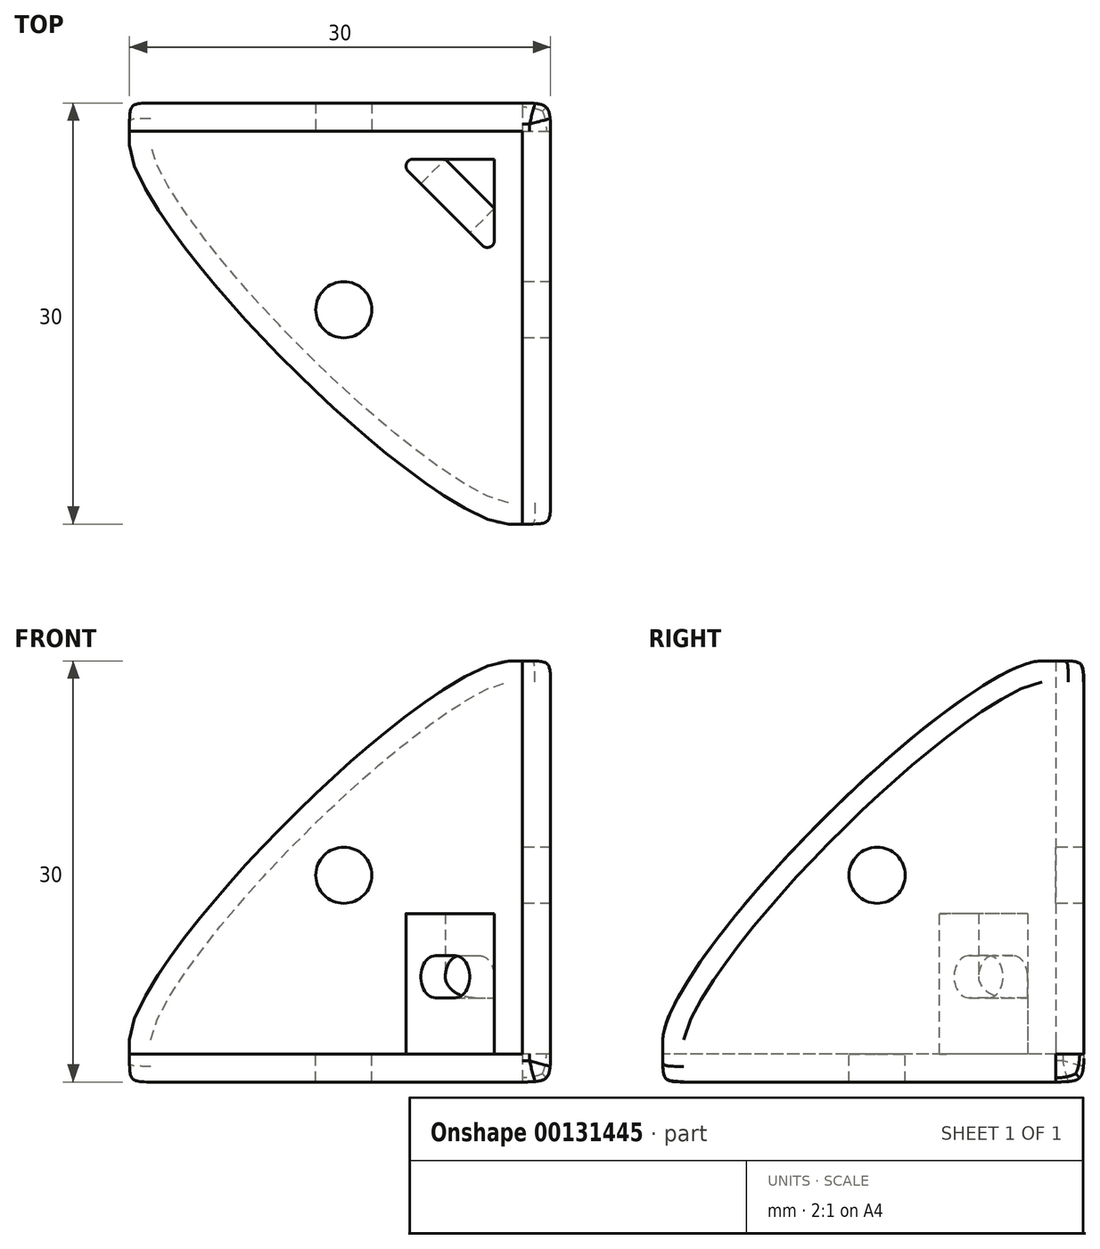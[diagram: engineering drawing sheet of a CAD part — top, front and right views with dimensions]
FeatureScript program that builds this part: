
annotation { "Feature Type Name" : "Feature", "Feature Type Description" : "" }
export const myFeature = defineFeature(function(context is Context, id is Id, definition is map)
    precondition{}
    {
        {
            var Q0;
            Q0=qCreatedBy(makeId("Top.planeOp"),FACE);
            var sketch = newSketch(context, id + "F0", { "sketchPlane" : qUnion([Q0])});
            skLineSegment(sketch, "E0.bottom", {"start": v(0, 0) * mm, "end": v(-30, 0) * mm});
            skLineSegment(sketch, "E0.top", {"start": v(0, -30) * mm, "end": v(-30, -30) * mm});
            skLineSegment(sketch, "E0.left", {"start": v(0, 0) * mm, "end": v(0, -30) * mm});
            skLineSegment(sketch, "E0.right", {"start": v(-30, 0) * mm, "end": v(-30, -30) * mm});
            skSolve(sketch);
        }
        {
            var Q0;
            Q0 = qSketchRegion(id + "F0", true);
            extrude(context, id + "F1", {"entities" : qUnion([Q0]), "depth" : 30 * mm});
        }
        {
            var Q0;
            Q0=makeQuery(id+"F1.opExtrude","CAP_FACE",FACE,{"disambiguationData":[OSD([sQuery(id+"F0.wireOp",EDGE,"E0.bottom"),sQuery(id+"F0.wireOp",EDGE,"E0.top"),sQuery(id+"F0.wireOp",EDGE,"E0.left"),sQuery(id+"F0.wireOp",EDGE,"E0.right")])],"isStart":false});
            var Q1;
            Q1=makeQuery(id+"F1.opExtrude","SWEPT_FACE",FACE,{"disambiguationData":[OSD([sQuery(id+"F0.wireOp",EDGE,"E0.right")])]});
            var Q2;
            Q2=makeQuery(id+"F1.opExtrude","SWEPT_FACE",FACE,{"disambiguationData":[OSD([sQuery(id+"F0.wireOp",EDGE,"E0.top")])]});
            shell(context, id + "F2", {"entities" : qUnion([Q0, Q1, Q2]), "thickness" : 2 * mm});
        }
        {
            var Q0;
            Q0=makeQuery(id+"F1.opExtrude","CAP_EDGE",EDGE,{"disambiguationData":[OSD([sQuery(id+"F0.wireOp",EDGE,"E0.right")])],"isStart":false});
            var Q1;
            Q1=makeQuery(id+"F1.opExtrude","CAP_EDGE",EDGE,{"disambiguationData":[OSD([sQuery(id+"F0.wireOp",EDGE,"E0.top")])],"isStart":false});
            var Q2;
            Q2=makeQuery(id+"F1.opExtrude","SWEPT_EDGE",EDGE,{"disambiguationData":[OSD([sQuery(id+"F0.wireOp",EDGE,"E0.top"),sQuery(id+"F0.wireOp",EDGE,"E0.right")])]});
            fillet(context, id + "F3", {"entities" : qUnion([Q0, Q1, Q2]), "radius" : 27 * mm, "tangentPropagation" : true, "rho" : 0.16, "crossSection" : FilletCrossSection.CONIC, "allowEdgeOverflow" : false});
        }
        {
            var Q0;
            Q0=makeQuery(id+"F1.opExtrude","CAP_EDGE",EDGE,{"disambiguationData":[OSD([sQuery(id+"F0.wireOp",EDGE,"E0.bottom")])],"isStart":true});
            var Q1;
            Q1=makeQuery(id+"F1.opExtrude","CAP_EDGE",EDGE,{"disambiguationData":[OSD([sQuery(id+"F0.wireOp",EDGE,"E0.left")])],"isStart":true});
            var Q2;
            Q2=makeQuery(id+"F1.opExtrude","SWEPT_EDGE",EDGE,{"disambiguationData":[OSD([sQuery(id+"F0.wireOp",EDGE,"E0.bottom"),sQuery(id+"F0.wireOp",EDGE,"E0.left")])]});
            fillet(context, id + "F4", {"entities" : qUnion([Q0, Q1, Q2]), "radius" : 2 * mm, "tangentPropagation" : true, "rho" : 0.7, "crossSection" : FilletCrossSection.CONIC, "allowEdgeOverflow" : false});
        }
        {
            var Q0;
            Q0=makeQuery(id+"F2.opShell","OFFSET_FACE",FACE,{"disambiguationData":[OSD([sQuery(id+"F0.wireOp",EDGE,"E0.bottom"),sQuery(id+"F0.wireOp",EDGE,"E0.top"),sQuery(id+"F0.wireOp",EDGE,"E0.left"),sQuery(id+"F0.wireOp",EDGE,"E0.right")])]});
            var sketch = newSketch(context, id + "F5", { "sketchPlane" : qUnion([Q0])});
            skLineSegment(sketch, "E1.0", {"start": v(-2, -2) * mm, "end": v(-30, -2) * mm});
            skLineSegment(sketch, "E2.0", {"start": v(-2, -2) * mm, "end": v(-2, -30) * mm});
            skLineSegment(sketch, "E3", {"start": v(-11, -4) * mm, "end": v(-4, -4) * mm});
            skLineSegment(sketch, "E4", {"start": v(-4, -4) * mm, "end": v(-4, -11) * mm});
            skLineSegment(sketch, "E5", {"start": v(-11, -4) * mm, "end": v(-4, -11) * mm});
            skSolve(sketch);
        }
        {
            var Q0;
            Q0=makeQuery(id+"F5.imprint","IMPRINT",FACE,{"disambiguationData":[TD([[makeQuery(id+"F5.imprint","IMPRINT",EDGE,{"derivedFrom":sQuery(id+"F5.wireOp",EDGE,"E3")}),-1.0]])]});
            extrude(context, id + "F6", {"entities" : qUnion([Q0]), "operationType" : NewBodyOperationType.ADD, "depth" : 4 * mm});
        }
        {
            var Q0;
            Q0=makeQuery(id+"F6.opExtrude","CAP_FACE",FACE,{"disambiguationData":[OSD([sQuery(id+"F5.wireOp",EDGE,"E3"),sQuery(id+"F5.wireOp",EDGE,"E4"),sQuery(id+"F5.wireOp",EDGE,"E5")])],"isStart":false});
            var sketch = newSketch(context, id + "F7", { "sketchPlane" : qUnion([Q0])});
            skLineSegment(sketch, "E6.0.0", {"start": v(-4, -4) * mm, "end": v(-11, -4) * mm});
            skLineSegment(sketch, "E6.0.1", {"start": v(-11, -4) * mm, "end": v(-4, -11) * mm});
            skLineSegment(sketch, "E6.0.2", {"start": v(-4, -11) * mm, "end": v(-4, -4) * mm});
            skLineSegment(sketch, "E7", {"start": v(-7.5, -4) * mm, "end": v(-4, -7.5) * mm});
            skSolve(sketch);
        }
        {
            var Q0;
            {var subQ0=sQuery(id+"F7.wireOp",EDGE,"E6.0.1");Q0=makeQuery(id+"F7.imprint","IMPRINT",FACE,{"disambiguationData":[TD([[makeQuery(id+"F7.imprint","IMPRINT",EDGE,{"derivedFrom":subQ0}),1.0]])]});}
            extrude(context, id + "F8", {"entities" : qUnion([Q0]), "operationType" : NewBodyOperationType.ADD, "depth" : 6 * mm});
        }
        {
            var Q0;
            Q0=makeQuery(id+"F8.opExtrude","SWEPT_FACE",FACE,{"disambiguationData":[OSD([sQuery(id+"F7.wireOp",EDGE,"E7")])]});
            var sketch = newSketch(context, id + "F9", { "sketchPlane" : qUnion([Q0])});
            skLineSegment(sketch, "E8.0", {"start": v(2.47, 6) * mm, "end": v(-2.47, 6) * mm});
            skLineSegment(sketch, "E9", {"start": v(2.47, 6) * mm, "end": v(2.47, 9) * mm});
            skLineSegment(sketch, "E10", {"start": v(2.47, 9) * mm, "end": v(-2.47, 9) * mm});
            skLineSegment(sketch, "E11", {"start": v(-2.47, 9) * mm, "end": v(-2.47, 6) * mm});
            skSolve(sketch);
        }
        {
            var Q0;
            Q0=makeQuery(id+"F9.imprint","IMPRINT",FACE,{"disambiguationData":[TD([[makeQuery(id+"F9.imprint","IMPRINT",EDGE,{"derivedFrom":sQuery(id+"F9.wireOp",EDGE,"E8.0")}),-1.0]])]});
            extrude(context, id + "F10", {"entities" : qUnion([Q0]), "operationType" : NewBodyOperationType.REMOVE, "endBound" : BoundingType.THROUGH_ALL, "oppositeDirection" : true, "depth" : 25 * mm});
        }
        {
            var Q0;
            Q0=makeQuery(id+"F2.opShell","OFFSET_FACE",FACE,{"disambiguationData":[OSD([sQuery(id+"F0.wireOp",EDGE,"E0.bottom"),sQuery(id+"F0.wireOp",EDGE,"E0.top"),sQuery(id+"F0.wireOp",EDGE,"E0.left"),sQuery(id+"F0.wireOp",EDGE,"E0.right")])]});
            var sketch = newSketch(context, id + "F11", { "sketchPlane" : qUnion([Q0])});
            skCircle(sketch, "E12", {"center": v(-14.73, -14.73) * mm, "radius": 2 * mm});
            skPoint(sketch, "E13.0", {"position": v(-2, -2) * mm});
            skLineSegment(sketch, "E14", {"start": v(-2, -2) * mm, "end": v(-14.73, -14.73) * mm, "construction": true});
            skFitSpline(sketch, "E15.0", {"points": [v(-3, -2) * mm, v(-12, -2) * mm, v(-21, -2) * mm, v(-30, -2) * mm]});
            skLineSegment(sketch, "E16.0.0", {"start": v(-30, -2) * mm, "end": v(-30, -3) * mm});
            skFitSpline(sketch, "E16.0.1", {"points": [v(-30, -3) * mm, v(-30, -3.57) * mm, v(-29.76, -4.35) * mm, v(-29.28, -5.33) * mm, v(-28.96, -5.97) * mm, v(-28.56, -6.68) * mm, v(-28.06, -7.46) * mm, v(-27.29, -8.66) * mm, v(-26.33, -9.98) * mm, v(-25.2, -11.41) * mm, v(-23.3, -13.78) * mm, v(-21.12, -16.2) * mm, v(-18.66, -18.66) * mm, v(-16.2, -21.12) * mm, v(-13.77, -23.3) * mm, v(-11.4, -25.2) * mm, v(-9.97, -26.34) * mm, v(-8.65, -27.3) * mm, v(-7.44, -28.07) * mm, v(-6.67, -28.57) * mm, v(-5.96, -28.97) * mm, v(-5.32, -29.28) * mm, v(-4.34, -29.76) * mm, v(-3.57, -30) * mm, v(-3, -30) * mm]});
            skLineSegment(sketch, "E16.0.2", {"start": v(-3, -30) * mm, "end": v(-2, -30) * mm});
            skLineSegment(sketch, "E16.0.3", {"start": v(-2, -30) * mm, "end": v(-2, -2) * mm});
            skLineSegment(sketch, "E16.0.4", {"start": v(-2, -2) * mm, "end": v(-30, -2) * mm});
            skSolve(sketch);
        }
        {
            var Q0;
            Q0=makeQuery(id+"F11.imprint","IMPRINT",FACE,{"disambiguationData":[TD([[makeQuery(id+"F11.imprint","IMPRINT",EDGE,{"derivedFrom":sQuery(id+"F11.wireOp",EDGE,"E12")}),1.0]])]});
            extrude(context, id + "F12", {"entities" : qUnion([Q0]), "operationType" : NewBodyOperationType.REMOVE, "endBound" : BoundingType.THROUGH_ALL, "oppositeDirection" : true, "depth" : 25 * mm});
        }
        {
            var Q0;
            Q0=makeQuery(id+"F8.boolean.opBoolean","MERGE",EDGE,{"derivedFrom":[makeQuery(id+"F6.opExtrude","SWEPT_EDGE",EDGE,{"disambiguationData":[OSD([sQuery(id+"F5.wireOp",EDGE,"E3"),sQuery(id+"F5.wireOp",EDGE,"E5")])]}),makeQuery(id+"F8.opExtrude","SWEPT_EDGE",EDGE,{"disambiguationData":[OSD([sQuery(id+"F7.wireOp",EDGE,"E6.0.0"),sQuery(id+"F7.wireOp",EDGE,"E6.0.1")])]})]});
            var Q1;
            Q1=makeQuery(id+"F8.boolean.opBoolean","MERGE",EDGE,{"derivedFrom":[makeQuery(id+"F6.opExtrude","SWEPT_EDGE",EDGE,{"disambiguationData":[OSD([sQuery(id+"F5.wireOp",EDGE,"E4"),sQuery(id+"F5.wireOp",EDGE,"E5")])]}),makeQuery(id+"F8.opExtrude","SWEPT_EDGE",EDGE,{"disambiguationData":[OSD([sQuery(id+"F7.wireOp",EDGE,"E6.0.1"),sQuery(id+"F7.wireOp",EDGE,"E6.0.2")])]})]});
            fillet(context, id + "F13", {"entities" : qUnion([Q0, Q1]), "radius" : 0.5 * mm, "tangentPropagation" : true, "allowEdgeOverflow" : false});
        }
        {
            var Q0;
            Q0=makeQuery(id+"F3.opFillet","BLEND_EDGE",EDGE,{"blendedFrom":[makeQuery(id+"F1.opExtrude","CAP_EDGE",EDGE,{"disambiguationData":[OSD([sQuery(id+"F0.wireOp",EDGE,"E0.right")])],"isStart":false}),makeQuery(id+"F1.opExtrude","SWEPT_FACE",FACE,{"disambiguationData":[OSD([sQuery(id+"F0.wireOp",EDGE,"E0.bottom")])]})],"blendedInto":[makeQuery(id+"F1.opExtrude","SWEPT_FACE",FACE,{"disambiguationData":[OSD([sQuery(id+"F0.wireOp",EDGE,"E0.bottom")])]})]});
            fillet(context, id + "F14", {"entities" : qUnion([Q0]), "radius" : 1.5 * mm, "tangentPropagation" : true, "rho" : 0.7, "crossSection" : FilletCrossSection.CONIC, "allowEdgeOverflow" : false});
        }
        {
            var Q0;
            Q0=makeQuery(id+"F10.boolean.opBoolean","COPY",EDGE,{"derivedFrom":makeQuery(id+"F10.opExtrude","SWEPT_EDGE",EDGE,{"disambiguationData":[OSD([sQuery(id+"F7.wireOp",EDGE,"E6.0.0"),sQuery(id+"F7.wireOp",EDGE,"E7"),sQuery(id+"F9.wireOp",EDGE,"E9"),sQuery(id+"F9.wireOp",EDGE,"E10")])]})});
            var Q1;
            Q1=makeQuery(id+"F10.boolean.opBoolean","COPY",EDGE,{"derivedFrom":makeQuery(id+"F10.opExtrude","SWEPT_EDGE",EDGE,{"disambiguationData":[OSD([sQuery(id+"F7.wireOp",EDGE,"E6.0.2"),sQuery(id+"F7.wireOp",EDGE,"E7"),sQuery(id+"F9.wireOp",EDGE,"E10"),sQuery(id+"F9.wireOp",EDGE,"E11")])]})});
            var Q2;
            Q2=makeQuery(id+"F10.boolean.opBoolean","COPY",EDGE,{"derivedFrom":makeQuery(id+"F10.opExtrude","SWEPT_EDGE",EDGE,{"disambiguationData":[OSD([sQuery(id+"F9.wireOp",EDGE,"E8.0"),sQuery(id+"F9.wireOp",EDGE,"E9")])]})});
            var Q3;
            Q3=makeQuery(id+"F10.boolean.opBoolean","COPY",EDGE,{"derivedFrom":makeQuery(id+"F10.opExtrude","SWEPT_EDGE",EDGE,{"disambiguationData":[OSD([sQuery(id+"F9.wireOp",EDGE,"E8.0"),sQuery(id+"F9.wireOp",EDGE,"E11")])]})});
            fillet(context, id + "F15", {"entities" : qUnion([Q0, Q1, Q2, Q3]), "radius" : 1.5 * mm, "allowEdgeOverflow" : false});
        }
        {
            var Q0;
            Q0=makeQuery(id+"F2.opShell","OFFSET_FACE",FACE,{"disambiguationData":[OSD([sQuery(id+"F0.wireOp",EDGE,"E0.left")])]});
            var sketch = newSketch(context, id + "F16", { "sketchPlane" : qUnion([Q0])});
            skLineSegment(sketch, "E17.0.0", {"start": v(30, 2) * mm, "end": v(30, 3) * mm});
            skFitSpline(sketch, "E17.0.1", {"points": [v(30, 3) * mm, v(30, 3.57) * mm, v(29.76, 4.35) * mm, v(29.28, 5.33) * mm, v(28.96, 5.97) * mm, v(28.56, 6.68) * mm, v(28.06, 7.46) * mm, v(27.29, 8.66) * mm, v(26.33, 9.98) * mm, v(25.2, 11.41) * mm, v(23.3, 13.78) * mm, v(21.12, 16.2) * mm, v(18.66, 18.66) * mm, v(16.2, 21.12) * mm, v(13.77, 23.3) * mm, v(11.4, 25.2) * mm, v(9.97, 26.34) * mm, v(8.65, 27.3) * mm, v(7.44, 28.07) * mm, v(6.67, 28.57) * mm, v(5.96, 28.97) * mm, v(5.32, 29.28) * mm, v(4.34, 29.76) * mm, v(3.57, 30) * mm, v(3, 30) * mm]});
            skLineSegment(sketch, "E17.0.2", {"start": v(3, 30) * mm, "end": v(2, 30) * mm});
            skLineSegment(sketch, "E17.0.3", {"start": v(2, 30) * mm, "end": v(2, 2) * mm});
            skLineSegment(sketch, "E17.0.4", {"start": v(2, 2) * mm, "end": v(30, 2) * mm});
            skLineSegment(sketch, "E18", {"start": v(2, 2) * mm, "end": v(14.73, 14.73) * mm});
            skCircle(sketch, "E19", {"center": v(14.73, 14.73) * mm, "radius": 2 * mm});
            skSolve(sketch);
        }
        {
            var Q0;
            Q0=makeQuery(id+"F16.imprint","IMPRINT",FACE,{"disambiguationData":[TD([[makeQuery(id+"F16.imprint","IMPRINT",EDGE,{"derivedFrom":sQuery(id+"F16.wireOp",EDGE,"E19")}),1.0]])]});
            extrude(context, id + "F17", {"entities" : qUnion([Q0]), "operationType" : NewBodyOperationType.REMOVE, "endBound" : BoundingType.THROUGH_ALL, "oppositeDirection" : true, "depth" : 25 * mm});
        }
        {
            var Q0;
            Q0=makeQuery(id+"F2.opShell","OFFSET_FACE",FACE,{"disambiguationData":[OSD([sQuery(id+"F0.wireOp",EDGE,"E0.bottom")])]});
            var sketch = newSketch(context, id + "F18", { "sketchPlane" : qUnion([Q0])});
            skLineSegment(sketch, "E20.0.0", {"start": v(-2, 30) * mm, "end": v(-3, 30) * mm});
            skFitSpline(sketch, "E20.0.1", {"points": [v(-3, 30) * mm, v(-3.57, 30) * mm, v(-4.35, 29.76) * mm, v(-5.33, 29.28) * mm, v(-5.97, 28.96) * mm, v(-6.68, 28.56) * mm, v(-7.46, 28.06) * mm, v(-8.66, 27.29) * mm, v(-9.98, 26.33) * mm, v(-11.41, 25.2) * mm, v(-13.78, 23.3) * mm, v(-16.2, 21.12) * mm, v(-18.66, 18.66) * mm, v(-21.12, 16.2) * mm, v(-23.3, 13.77) * mm, v(-25.2, 11.4) * mm, v(-26.34, 9.97) * mm, v(-27.3, 8.65) * mm, v(-28.07, 7.44) * mm, v(-28.57, 6.67) * mm, v(-28.97, 5.96) * mm, v(-29.28, 5.32) * mm, v(-29.76, 4.34) * mm, v(-30, 3.57) * mm, v(-30, 3) * mm]});
            skLineSegment(sketch, "E20.0.2", {"start": v(-30, 3) * mm, "end": v(-30, 2) * mm});
            skLineSegment(sketch, "E20.0.3", {"start": v(-30, 2) * mm, "end": v(-2, 2) * mm});
            skLineSegment(sketch, "E20.0.4", {"start": v(-2, 2) * mm, "end": v(-2, 30) * mm});
            skLineSegment(sketch, "E21", {"start": v(-2, 2) * mm, "end": v(-14.73, 14.73) * mm});
            skCircle(sketch, "E22", {"center": v(-14.73, 14.73) * mm, "radius": 2 * mm});
            skSolve(sketch);
        }
        {
            var Q0;
            Q0=makeQuery(id+"F18.imprint","IMPRINT",FACE,{"disambiguationData":[TD([[makeQuery(id+"F18.imprint","IMPRINT",EDGE,{"derivedFrom":sQuery(id+"F18.wireOp",EDGE,"E22")}),1.0]])]});
            extrude(context, id + "F19", {"entities" : qUnion([Q0]), "operationType" : NewBodyOperationType.REMOVE, "endBound" : BoundingType.THROUGH_ALL, "oppositeDirection" : true, "depth" : 25 * mm});
        }
    });
